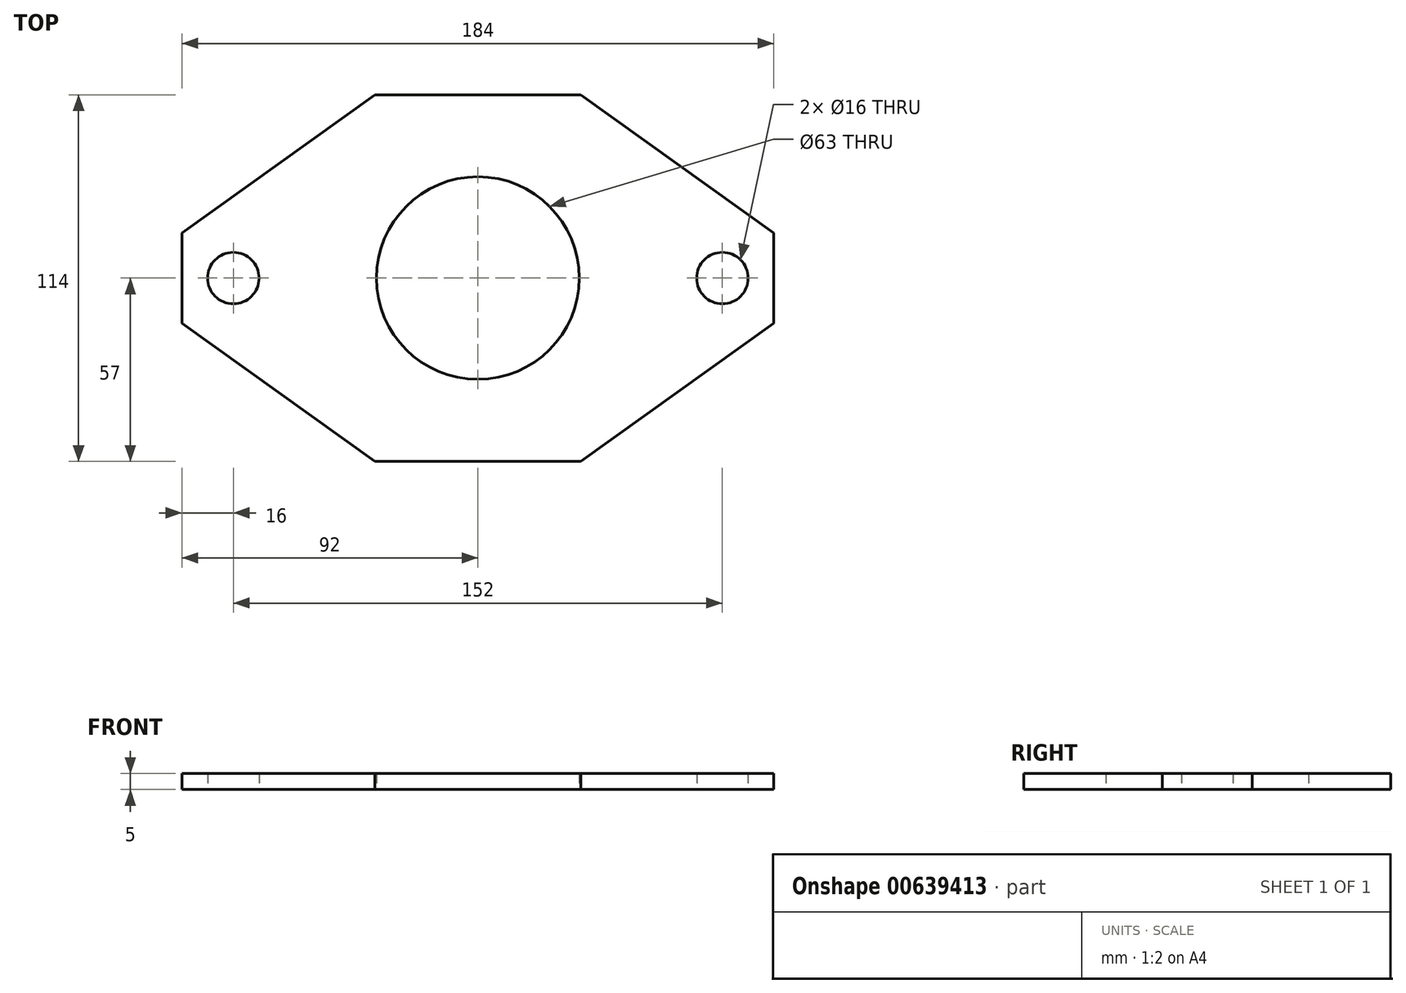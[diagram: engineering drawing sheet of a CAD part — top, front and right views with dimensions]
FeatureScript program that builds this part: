
annotation { "Feature Type Name" : "Feature", "Feature Type Description" : "" }
export const myFeature = defineFeature(function(context is Context, id is Id, definition is map)
    precondition{}
    {
        {
            var Q0;
            Q0=qCreatedBy(makeId("Top.planeOp"),FACE);
            var sketch = newSketch(context, id + "F0", { "sketchPlane" : qUnion([Q0])});
            skLineSegment(sketch, "E0.bottom", {"start": v(60, 0) * mm, "end": v(124, 0) * mm});
            skLineSegment(sketch, "E0.top", {"start": v(60, 114) * mm, "end": v(124, 114) * mm});
            skLineSegment(sketch, "E0.left", {"start": v(0, 43) * mm, "end": v(0, 71) * mm});
            skLineSegment(sketch, "E0.right", {"start": v(184, 43) * mm, "end": v(184, 71) * mm});
            skLineSegment(sketch, "E1", {"start": v(124, 0) * mm, "end": v(184, 43) * mm});
            skLineSegment(sketch, "E2.MirrorCS", {"start": v(124, 114) * mm, "end": v(184, 71) * mm});
            skLineSegment(sketch, "E3.MirrorCS", {"start": v(60, 114) * mm, "end": v(0, 71) * mm});
            skLineSegment(sketch, "E4.MirrorCS", {"start": v(60, 0) * mm, "end": v(0, 43) * mm});
            skCircle(sketch, "E5", {"center": v(92, 57) * mm, "radius": 31.5 * mm});
            skCircle(sketch, "E6", {"center": v(16, 57) * mm, "radius": 8 * mm});
            skCircle(sketch, "E7", {"center": v(168, 57) * mm, "radius": 8 * mm});
            skSolve(sketch);
        }
        {
            var Q0;
            Q0=makeQuery(id+"F0.imprint","IMPRINT",FACE,{"disambiguationData":[TD([[makeQuery(id+"F0.imprint","IMPRINT",EDGE,{"derivedFrom":sQuery(id+"F0.wireOp",EDGE,"E0.bottom")}),1.0]])]});
            extrude(context, id + "F1", {"entities" : qUnion([Q0]), "depth" : 5 * mm, "offsetDistance" : 25 * mm});
        }
    });
